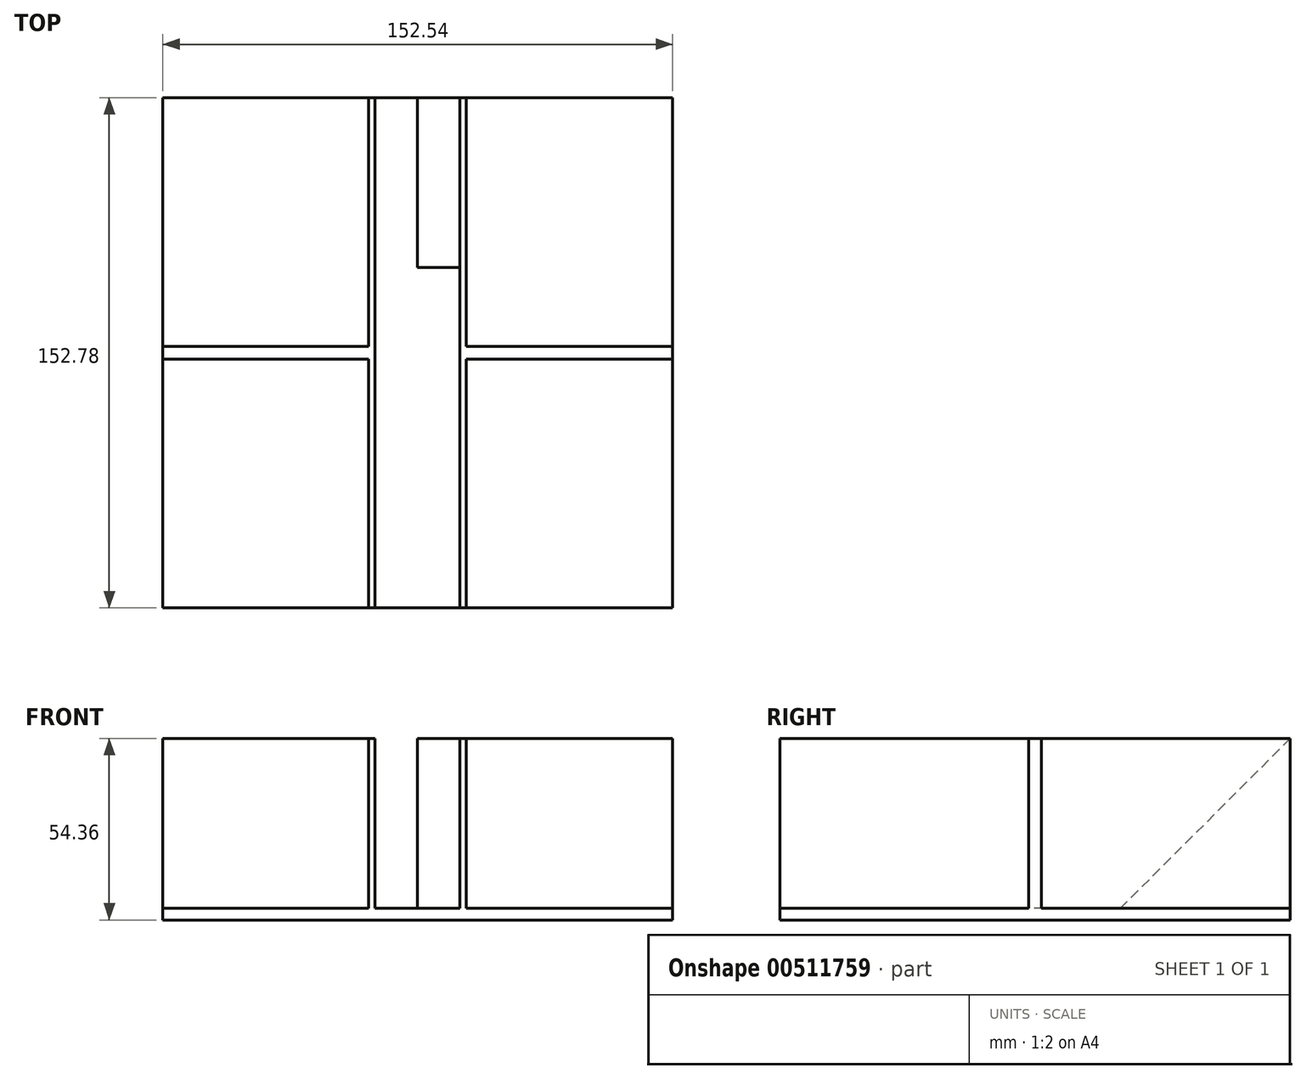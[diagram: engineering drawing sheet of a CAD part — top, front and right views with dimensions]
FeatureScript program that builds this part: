
annotation { "Feature Type Name" : "Feature", "Feature Type Description" : "" }
export const myFeature = defineFeature(function(context is Context, id is Id, definition is map)
    precondition{}
    {
        {
            var Q0;
            Q0=qCreatedBy(makeId("Top.planeOp"),FACE);
            var sketch = newSketch(context, id + "F0", { "sketchPlane" : qUnion([Q0])});
            skLineSegment(sketch, "E0.bottom", {"start": v(-76.15, 76.39) * mm, "end": v(76.39, 76.39) * mm});
            skLineSegment(sketch, "E0.top", {"start": v(-76.15, -76.39) * mm, "end": v(76.39, -76.39) * mm});
            skLineSegment(sketch, "E0.left", {"start": v(-76.15, 76.39) * mm, "end": v(-76.15, -76.39) * mm});
            skLineSegment(sketch, "E0.right", {"start": v(76.39, 76.39) * mm, "end": v(76.39, -76.39) * mm});
            skSolve(sketch);
        }
        {
            var Q0;
            Q0=makeQuery(id+"F0.imprint","IMPRINT",FACE,{"disambiguationData":[TD([[makeQuery(id+"F0.imprint","IMPRINT",EDGE,{"derivedFrom":sQuery(id+"F0.wireOp",EDGE,"E0.bottom")}),-1.0]])]});
            extrude(context, id + "F1", {"entities" : qUnion([Q0]), "depth" : 3.56 * mm});
        }
        {
            var Q0;
            Q0=makeQuery(id+"F1.opExtrude","CAP_FACE",FACE,{"disambiguationData":[OSD([sQuery(id+"F0.wireOp",EDGE,"E0.bottom"),sQuery(id+"F0.wireOp",EDGE,"E0.top"),sQuery(id+"F0.wireOp",EDGE,"E0.left"),sQuery(id+"F0.wireOp",EDGE,"E0.right")])],"isStart":false});
            var sketch = newSketch(context, id + "F2", { "sketchPlane" : qUnion([Q0])});
            skLineSegment(sketch, "E1.bottom", {"start": v(0, 76.39) * mm, "end": v(12.7, 76.39) * mm});
            skLineSegment(sketch, "E1.top", {"start": v(0, 25.59) * mm, "end": v(12.7, 25.59) * mm});
            skLineSegment(sketch, "E1.left", {"start": v(0, 76.39) * mm, "end": v(0, 25.59) * mm});
            skLineSegment(sketch, "E1.right", {"start": v(12.7, 76.39) * mm, "end": v(12.7, 25.59) * mm});
            skSolve(sketch);
        }
        {
            var Q0;
            Q0=makeQuery(id+"F2.imprint","IMPRINT",FACE,{"disambiguationData":[TD([[makeQuery(id+"F2.imprint","IMPRINT",EDGE,{"derivedFrom":sQuery(id+"F2.wireOp",EDGE,"E1.bottom")}),-1.0]])]});
            extrude(context, id + "F3", {"entities" : qUnion([Q0]), "operationType" : NewBodyOperationType.ADD, "depth" : 50.8 * mm, "offsetDistance" : 25.4 * mm});
        }
        {
            var Q0;
            Q0=makeQuery(id+"F3.opExtrude","SWEPT_FACE",FACE,{"disambiguationData":[OSD([sQuery(id+"F2.wireOp",EDGE,"E1.right")])]});
            var sketch = newSketch(context, id + "F4", { "sketchPlane" : qUnion([Q0])});
            skLineSegment(sketch, "E2", {"start": v(76.39, 54.36) * mm, "end": v(25.59, 3.56) * mm});
            skSolve(sketch);
        }
        {
            var Q0;
            Q0=makeQuery(id+"F4.imprint","IMPRINT",FACE,{"disambiguationData":[TD([[makeQuery(id+"F4.imprint","IMPRINT",EDGE,{"derivedFrom":sQuery(id+"F4.wireOp",EDGE,"E2")}),-1.0]])]});
            extrude(context, id + "F5", {"entities" : qUnion([Q0]), "operationType" : NewBodyOperationType.REMOVE, "oppositeDirection" : true, "depth" : 25.4 * mm, "offsetDistance" : 25.4 * mm});
        }
        {
            var Q0;
            Q0=makeQuery(id+"F1.opExtrude","CAP_FACE",FACE,{"disambiguationData":[OSD([sQuery(id+"F0.wireOp",EDGE,"E0.bottom"),sQuery(id+"F0.wireOp",EDGE,"E0.top"),sQuery(id+"F0.wireOp",EDGE,"E0.left"),sQuery(id+"F0.wireOp",EDGE,"E0.right")])],"isStart":false});
            var sketch = newSketch(context, id + "F6", { "sketchPlane" : qUnion([Q0])});
            skLineSegment(sketch, "E3", {"start": v(12.7, 76.39) * mm, "end": v(12.7, 0) * mm});
            skLineSegment(sketch, "E4", {"start": v(12.7, 0) * mm, "end": v(76.39, 0) * mm});
            skLineSegment(sketch, "E5", {"start": v(12.7, 0) * mm, "end": v(12.7, -76.39) * mm});
            skLineSegment(sketch, "E6", {"start": v(-12.7, 76.39) * mm, "end": v(-12.7, 0) * mm});
            skLineSegment(sketch, "E7", {"start": v(-12.7, 0) * mm, "end": v(-76.15, 0) * mm});
            skLineSegment(sketch, "E8", {"start": v(-12.7, 0) * mm, "end": v(-12.7, -76.39) * mm});
            skLineSegment(sketch, "E9", {"start": v(-14.6, 76.39) * mm, "end": v(-14.6, 0) * mm});
            skLineSegment(sketch, "E10.MirrorCS", {"start": v(-14.6, -76.39) * mm, "end": v(-14.6, 0) * mm});
            skLineSegment(sketch, "E11.MirrorCS", {"start": v(14.6, 76.39) * mm, "end": v(14.6, 0) * mm});
            skLineSegment(sketch, "E12.MirrorCS", {"start": v(14.6, -76.39) * mm, "end": v(14.6, 0) * mm});
            skLineSegment(sketch, "E13", {"start": v(-76.15, 1.9) * mm, "end": v(-14.6, 1.9) * mm});
            skLineSegment(sketch, "E14.MirrorCS", {"start": v(-76.15, -1.9) * mm, "end": v(-14.6, -1.9) * mm});
            skLineSegment(sketch, "E15.MirrorCS", {"start": v(76.15, 1.9) * mm, "end": v(14.6, 1.9) * mm});
            skLineSegment(sketch, "E16.MirrorCS", {"start": v(76.15, -1.9) * mm, "end": v(14.6, -1.9) * mm});
            skLineSegment(sketch, "E17", {"start": v(76.15, 1.9) * mm, "end": v(76.39, 1.9) * mm});
            skLineSegment(sketch, "E18", {"start": v(76.39, 1.9) * mm, "end": v(76.39, 0) * mm});
            skLineSegment(sketch, "E19", {"start": v(76.15, -1.9) * mm, "end": v(76.39, -1.9) * mm});
            skLineSegment(sketch, "E20", {"start": v(76.39, -1.9) * mm, "end": v(76.39, 0) * mm});
            skSolve(sketch);
        }
        {
            var Q0;
            {var subQ5=sQuery(id+"F6.wireOp",EDGE,"E13");Q0=makeQuery(id+"F6.imprint","IMPRINT",FACE,{"disambiguationData":[TD([[makeQuery(id+"F6.imprint","IMPRINT",EDGE,{"derivedFrom":subQ5}),-1.0]])]});}
            var Q1;
            {var subQ5=sQuery(id+"F6.wireOp",EDGE,"E14.MirrorCS");Q1=makeQuery(id+"F6.imprint","IMPRINT",FACE,{"disambiguationData":[TD([[makeQuery(id+"F6.imprint","IMPRINT",EDGE,{"derivedFrom":subQ5}),1.0]])]});}
            var Q2;
            {var subQ7=sQuery(id+"F6.wireOp",EDGE,"E6");Q2=makeQuery(id+"F6.imprint","IMPRINT",FACE,{"disambiguationData":[TD([[makeQuery(id+"F6.imprint","IMPRINT",EDGE,{"derivedFrom":subQ7}),-1.0]])]});}
            var Q3;
            {var subQ4=sQuery(id+"F6.wireOp",EDGE,"E8");Q3=makeQuery(id+"F6.imprint","IMPRINT",FACE,{"disambiguationData":[TD([[makeQuery(id+"F6.imprint","IMPRINT",EDGE,{"derivedFrom":subQ4}),-1.0]])]});}
            var Q4;
            {var subQ0=sQuery(id+"F6.wireOp",EDGE,"E11.MirrorCS");var subQ6=makeQuery(id+"F6.imprint","INTERSECT",VERTEX,{"derivedFrom":[subQ0,sQuery(id+"F6.wireOp",EDGE,"E15.MirrorCS")]});Q4=makeQuery(id+"F6.imprint","IMPRINT",FACE,{"disambiguationData":[TD([[makeQuery(id+"F6.imprint","IMPRINT",EDGE,{"disambiguationData":[TD([[subQ6,-1.0]])],"derivedFrom":subQ0}),-1.0]])]});}
            var Q5;
            {var subQ6=sQuery(id+"F6.wireOp",EDGE,"E5");Q5=makeQuery(id+"F6.imprint","IMPRINT",FACE,{"disambiguationData":[TD([[makeQuery(id+"F6.imprint","IMPRINT",EDGE,{"derivedFrom":subQ6}),1.0]])]});}
            var Q6;
            {var subQ0=sQuery(id+"F6.wireOp",EDGE,"E15.MirrorCS");Q6=makeQuery(id+"F6.imprint","IMPRINT",FACE,{"disambiguationData":[TD([[makeQuery(id+"F6.imprint","IMPRINT",EDGE,{"derivedFrom":subQ0}),1.0]])]});}
            var Q7;
            {var subQ0=sQuery(id+"F6.wireOp",EDGE,"E16.MirrorCS");Q7=makeQuery(id+"F6.imprint","IMPRINT",FACE,{"disambiguationData":[TD([[makeQuery(id+"F6.imprint","IMPRINT",EDGE,{"derivedFrom":subQ0}),-1.0]])]});}
            extrude(context, id + "F7", {"entities" : qUnion([Q0, Q1, Q2, Q3, Q4, Q5, Q6, Q7]), "operationType" : NewBodyOperationType.ADD, "depth" : 50.8 * mm, "offsetDistance" : 25.4 * mm});
        }
    });
